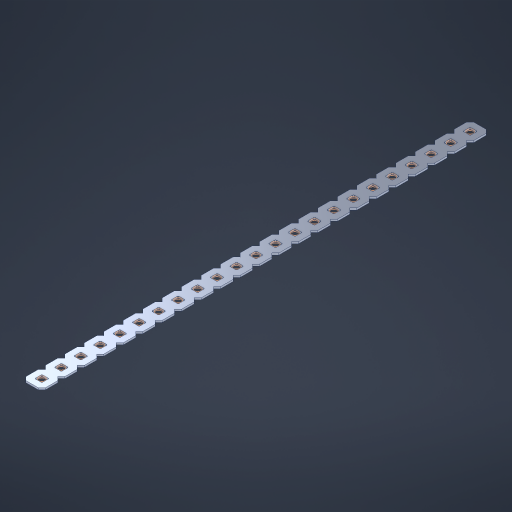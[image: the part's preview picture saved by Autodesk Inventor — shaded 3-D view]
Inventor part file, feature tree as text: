
AUTODESK INVENTOR PART (.ipt)
format: ipt  version: 2023 (Build 270158000, 158)  size: 555,008 bytes
history: native  units: in
note: dims shown in document units (in); Inventor stores cm internally (conversion verified against a paired STEP export)
features: other x24, extrude x22, sketch x2, pattern_linear x1
ambient origin geometry x8: Origin, YZ Plane, XZ Plane, XY Plane, X Axis, Y Axis, Z Axis, Center Point
bodies: Solid1 (feature_tree), Body (feature_tree)
feature tree (49):
  pattern_linear  "Rectangular Pattern1"  Spacing1=0.09in  [1 undecoded]
  sketch  "Sketch1"  dims[d1=0.5in]
  sketch  "Sketch2"  dims[d2=0.182in d3=0.09in d4=0.09in d5=0.09in d6=0.09in d7=0.09in d8=0.09in d9=0.09in d10=0.09in d11=0.02in d13=0.0in d14=0.172in d15=0.0625in d16=0.0in d19=0.5in d22=0.5in]
  other  "Srf1"
  other  "Srf126"
  other  "Srf127"
  other  "Srf128"
  other  "Srf129"
  other  "Srf130"
  other  "Srf131"
  other  "Srf250"
  other  "Srf251"
  other  "Srf252"
  other  "Srf253"
  other  "Srf254"
  other  "Srf255"
  other  "Srf256"
  other  "Srf257"
  other  "Srf258"
  other  "Srf259"
  other  "Srf260"
  other  "Srf261"
  other  "Srf262"
  other  "Srf263"
  other  "Srf264"
  other  "Srf265"
  other  "Circle"
  extrude  "ExtrusionSrf126"  Depth=0.09in
  extrude  "ExtrusionSrf127"  Depth=0.09in
  extrude  "ExtrusionSrf128"  Depth=0.09in
  extrude  "ExtrusionSrf129"  Depth=0.09in
  extrude  "ExtrusionSrf130"  Depth=0.09in
  extrude  "ExtrusionSrf131"  Depth=0.09in
  extrude  "ExtrusionSrf250"  Depth=0.09in
  extrude  "ExtrusionSrf251"  Depth=0.02in
  extrude  "ExtrusionSrf252"  TaperAngle=0.0deg  [1 undecoded]
  extrude  "ExtrusionSrf253"  Depth=0.5in
  extrude  "ExtrusionSrf254"  Depth=0.5in TaperAngle=0.0deg
  extrude  "ExtrusionSrf255"  Depth=0.5in
  extrude  "ExtrusionSrf256"  Depth=0.5in
  extrude  "ExtrusionSrf257"  [1 undecoded]
  extrude  "ExtrusionSrf258"  [1 undecoded]
  extrude  "ExtrusionSrf259"  [1 undecoded]
  extrude  "ExtrusionSrf260"  [1 undecoded]
  extrude  "ExtrusionSrf261"  [1 undecoded]
  extrude  "ExtrusionSrf262"  [1 undecoded]
  extrude  "ExtrusionSrf263"  [1 undecoded]
  extrude  "ExtrusionSrf264"  [1 undecoded]
  extrude  "ExtrusionSrf265"  [1 undecoded]
note: 11 required parameter values undecoded (feature->parameter linkage not recoverable at this tier; creation-order binding heuristic only, values carry confidence <= 0.55)
